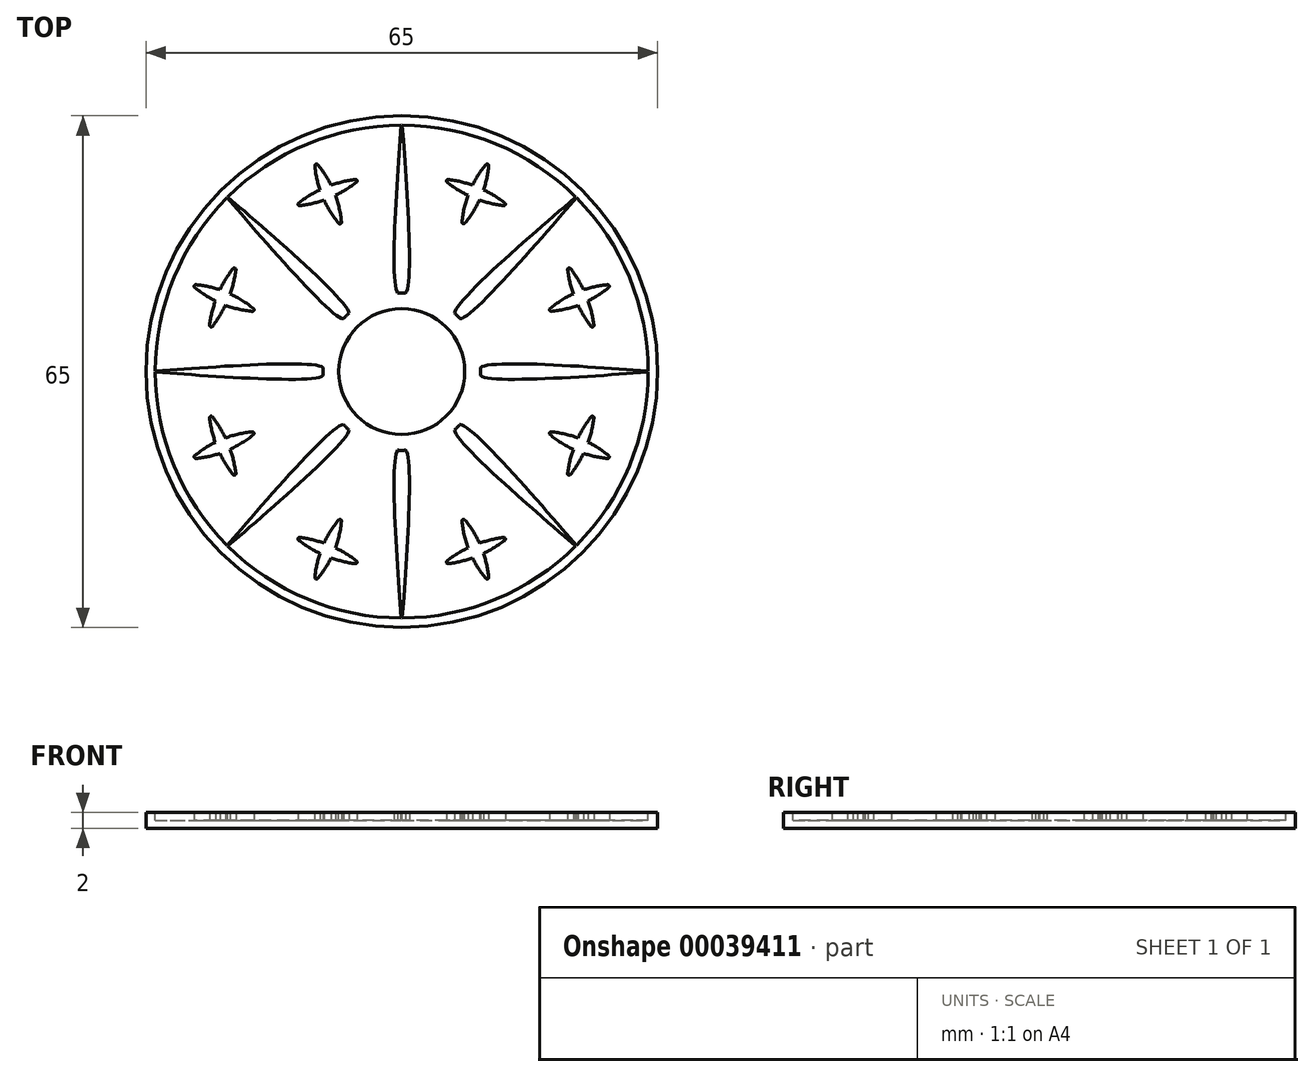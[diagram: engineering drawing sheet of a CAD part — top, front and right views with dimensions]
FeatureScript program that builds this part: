
annotation { "Feature Type Name" : "Feature", "Feature Type Description" : "" }
export const myFeature = defineFeature(function(context is Context, id is Id, definition is map)
    precondition{}
    {
        {
            var Q0;
            Q0=qCreatedBy(makeId("Top.planeOp"),FACE);
            var sketch = newSketch(context, id + "F0", { "sketchPlane" : qUnion([Q0])});
            skCircle(sketch, "E0", {"center": v(0, 0) * mm, "radius": 32.5 * mm});
            skSolve(sketch);
        }
        {
            var Q0;
            Q0=qSketchRegion(id+"F0",true);
            extrude(context, id + "F1", {"entities" : qUnion([Q0]), "depth" : 2 * mm});
        }
        {
            var Q0;
            Q0=makeQuery(id+"F1.opExtrude","CAP_FACE",FACE,{"disambiguationData":[OSD([sQuery(id+"F0.wireOp",EDGE,"E0")])],"isStart":false});
            var sketch = newSketch(context, id + "F2", { "sketchPlane" : qUnion([Q0])});
            skCircle(sketch, "E1", {"center": v(0, 0) * mm, "radius": 31.3 * mm});
            skCircle(sketch, "E2", {"center": v(0, 0) * mm, "radius": 8 * mm});
            skSolve(sketch);
        }
        {
            var Q0;
            Q0=qSketchRegion(id+"F2",true);
            extrude(context, id + "F3", {"entities" : qUnion([Q0]), "operationType" : NewBodyOperationType.REMOVE, "oppositeDirection" : true, "depth" : 1 * mm});
        }
        {
            var Q0;
            Q0=makeQuery(id+"F3.boolean.opBoolean","COPY",FACE,{"derivedFrom":makeQuery(id+"F3.opExtrude","CAP_FACE",FACE,{"disambiguationData":[OSD([sQuery(id+"F2.wireOp",EDGE,"E1"),sQuery(id+"F2.wireOp",EDGE,"E2")])],"isStart":false})});
            var sketch = newSketch(context, id + "F4", { "sketchPlane" : qUnion([Q0])});
            skArc(sketch, "E3", {"start": v(0.5, 9.99) * mm, "mid": v(0, 10) * mm, "end": v(-0.5, 9.99) * mm});
            skFitSpline(sketch, "E4", {"points": [v(-0.5, 9.99) * mm, v(0, 32) * mm], "startDerivative": vector(-3.57, 3.57) * mm, "endDerivative": vector(1.05, 13.85) * mm});
            skFitSpline(sketch, "E5", {"points": [v(0, 32) * mm, v(0.5, 9.99) * mm], "startDerivative": vector(1.05, -13.85) * mm, "endDerivative": vector(-3.57, -3.57) * mm});
            skArc(sketch, "E6", {"start": v(10.69, 26.3) * mm, "mid": v(9.75, 25.04) * mm, "end": v(8.98, 23.68) * mm});
            skArc(sketch, "E7", {"start": v(8.01, 18.84) * mm, "mid": v(9.04, 20.26) * mm, "end": v(9.88, 21.8) * mm});
            skLineSegment(sketch, "E8", {"start": v(0, 0) * mm, "end": v(0, 8) * mm, "construction": true});
            skLineSegment(sketch, "E9", {"start": v(0, 0) * mm, "end": v(15.23, 36.78) * mm, "construction": true});
            skLineSegment(sketch, "E10", {"start": v(-1.69, 11.18) * mm, "end": v(-0.5, 9.99) * mm, "construction": true});
            skLineSegment(sketch, "E11", {"start": v(1.69, 11.18) * mm, "end": v(0.5, 9.99) * mm, "construction": true});
            skArc(sketch, "E12", {"start": v(13.1, 21.43) * mm, "mid": v(11.79, 22.33) * mm, "end": v(10.4, 23.09) * mm});
            skArc(sketch, "E13", {"start": v(5.75, 24.05) * mm, "mid": v(7.04, 23.15) * mm, "end": v(8.43, 22.4) * mm});
            skArc(sketch, "E14", {"start": v(13.3, 21.2) * mm, "mid": v(9.4, 23.2) * mm, "end": v(5.22, 24.48) * mm, "construction": true});
            skPoint(sketch, "E15.visualSharp", {"position": v(5.22, 24.48) * mm});
            skArc(sketch, "E15.filletArc", {"start": v(5.9, 24.4) * mm, "mid": v(5.68, 24.29) * mm, "end": v(5.75, 24.05) * mm});
            skPoint(sketch, "E16.visualSharp", {"position": v(13.61, 21) * mm});
            skArc(sketch, "E16.filletArc", {"start": v(13.29, 21.2) * mm, "mid": v(13.22, 21.04) * mm, "end": v(13.3, 21.2) * mm});
            skArc(sketch, "E17.filletArc", {"start": v(12.94, 21.07) * mm, "mid": v(13.15, 21.2) * mm, "end": v(13.1, 21.43) * mm});
            skPoint(sketch, "E18.visualSharp", {"position": v(11.08, 26.75) * mm});
            skArc(sketch, "E18.filletArc", {"start": v(11.04, 26.15) * mm, "mid": v(10.92, 26.35) * mm, "end": v(10.69, 26.3) * mm});
            skPoint(sketch, "E19.visualSharp", {"position": v(7.62, 18.39) * mm});
            skArc(sketch, "E19.filletArc", {"start": v(7.66, 18.99) * mm, "mid": v(7.78, 18.78) * mm, "end": v(8.01, 18.84) * mm});
            skArc(sketch, "E20.filletArc", {"start": v(0.2, 29.4) * mm, "mid": v(0, 29.58) * mm, "end": v(-0.2, 29.4) * mm});
            skArc(sketch, "E21.trimOffspring", {"start": v(8.98, 23.68) * mm, "mid": v(7.46, 24.12) * mm, "end": v(5.9, 24.4) * mm});
            skArc(sketch, "E22.trimOffspring", {"start": v(8.43, 22.4) * mm, "mid": v(7.93, 20.72) * mm, "end": v(7.66, 18.99) * mm});
            skArc(sketch, "E23.trimOffspring", {"start": v(9.88, 21.8) * mm, "mid": v(11.4, 21.35) * mm, "end": v(12.94, 21.07) * mm});
            skArc(sketch, "E24.trimOffspring", {"start": v(10.4, 23.09) * mm, "mid": v(10.8, 24.6) * mm, "end": v(11.04, 26.15) * mm});
            skSolve(sketch);
        }
        {
            var Q0;
            Q0=qSketchRegion(id+"F4",true);
            var Q1;
            Q1=makeQuery(id+"F3.boolean.opBoolean","SPLIT",FACE,{"disambiguationData":[TD([makeQuery(id+"F3.opExtrude","SWEPT_FACE",FACE,{"disambiguationData":[OSD([sQuery(id+"F2.wireOp",EDGE,"E2")])]})])],"derivedFrom":makeQuery(id+"F1.opExtrude","CAP_FACE",FACE,{"disambiguationData":[OSD([sQuery(id+"F0.wireOp",EDGE,"E0")])],"isStart":false})});
            extrude(context, id + "F5", {"entities" : qUnion([Q0]), "operationType" : NewBodyOperationType.ADD, "endBound" : BoundingType.UP_TO_SURFACE, "endBoundEntityFace" : qUnion([Q1]), "depth" : 25 * mm});
        }
        {
            var Q0;
            Q0=makeQuery(id+"F1.opExtrude","SWEPT_BODY",BODY,{"disambiguationData":[OSD([sQuery(id+"F0.wireOp",EDGE,"E0")])]});
            var Q1;
            Q1=makeQuery(id+"F1.opExtrude","SWEPT_FACE",FACE,{"disambiguationData":[OSD([sQuery(id+"F0.wireOp",EDGE,"E0")])]});
            circularPattern(context, id + "F6", {"operationType" : NewBodyOperationType.ADD, "entities" : qUnion([Q0]), "axis" : qUnion([Q1]), "angle" : 360 * degree, "instanceCount" : 8, "equalSpace" : true});
        }
    });
